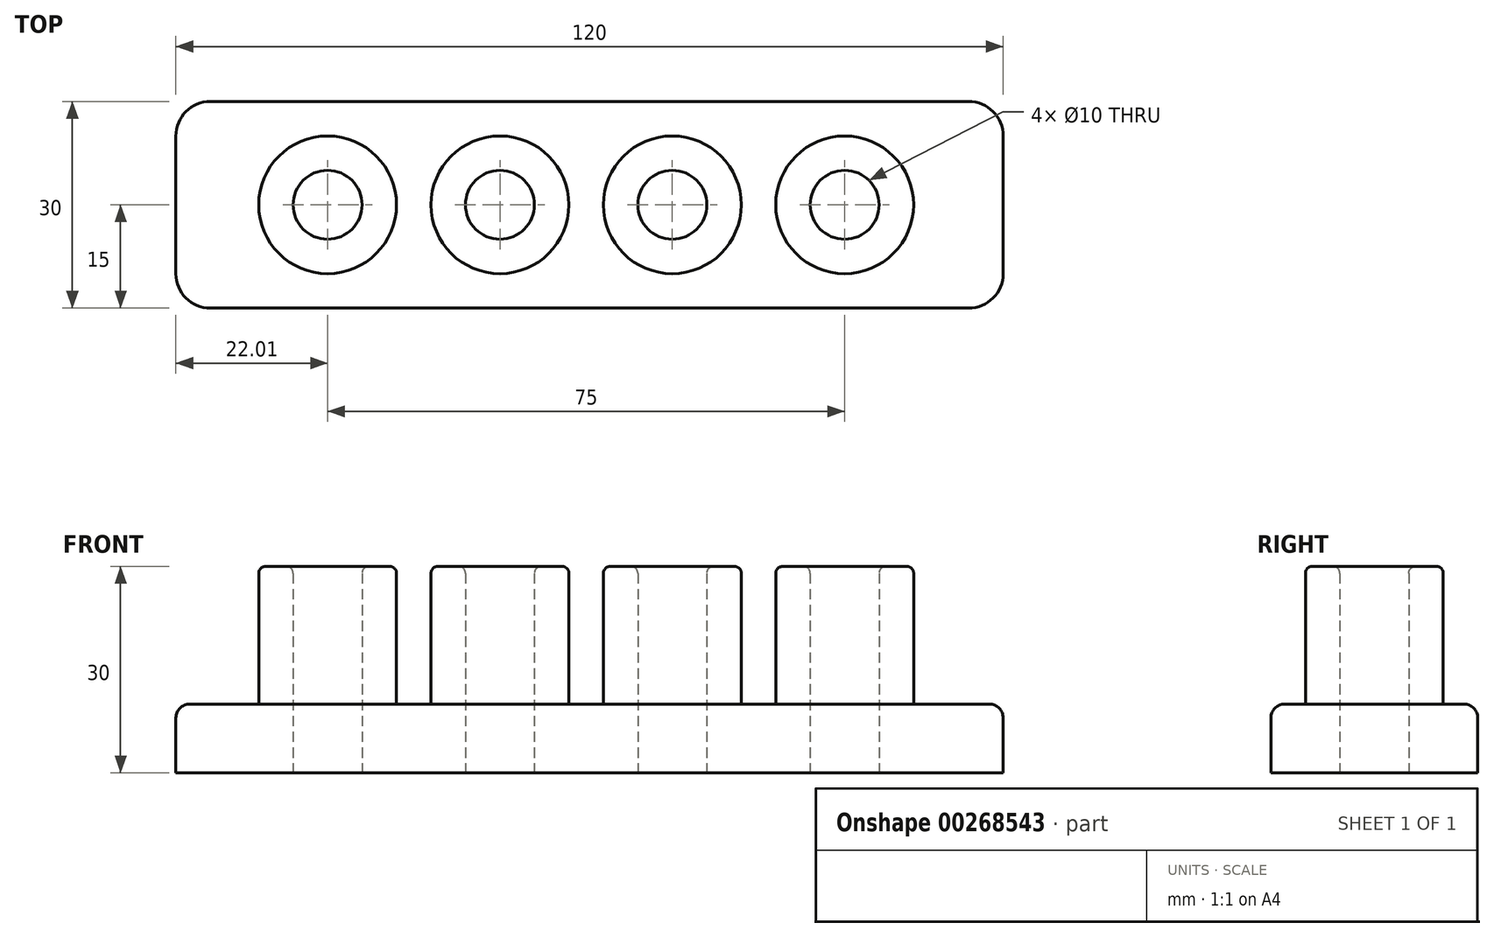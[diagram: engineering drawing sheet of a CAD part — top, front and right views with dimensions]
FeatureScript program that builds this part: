
annotation { "Feature Type Name" : "Feature", "Feature Type Description" : "" }
export const myFeature = defineFeature(function(context is Context, id is Id, definition is map)
    precondition{}
    {
        {
            var Q0;
            Q0=qCreatedBy(makeId("Top.planeOp"),FACE);
            var sketch = newSketch(context, id + "F0", { "sketchPlane" : qUnion([Q0])});
            skCircle(sketch, "E0", {"center": v(-25, 0) * mm, "radius": 10 * mm});
            skCircle(sketch, "E1", {"center": v(0, 0) * mm, "radius": 10 * mm});
            skCircle(sketch, "E2", {"center": v(25, 0) * mm, "radius": 10 * mm});
            skCircle(sketch, "E3", {"center": v(50, 0) * mm, "radius": 10 * mm});
            skLineSegment(sketch, "E4.bottom", {"start": v(-47, 15) * mm, "end": v(73, 15) * mm});
            skLineSegment(sketch, "E4.top", {"start": v(-47, -15) * mm, "end": v(73, -15) * mm});
            skLineSegment(sketch, "E4.left", {"start": v(-47, 15) * mm, "end": v(-47, -15) * mm});
            skLineSegment(sketch, "E4.right", {"start": v(73, 15) * mm, "end": v(73, -15) * mm});
            skCircle(sketch, "E5", {"center": v(-25, 0) * mm, "radius": 5 * mm});
            skCircle(sketch, "E6", {"center": v(0, 0) * mm, "radius": 5 * mm});
            skCircle(sketch, "E7", {"center": v(25, 0) * mm, "radius": 5 * mm});
            skCircle(sketch, "E8", {"center": v(50, 0) * mm, "radius": 5 * mm});
            skSolve(sketch);
        }
        {
            var Q0;
            Q0=makeQuery(id+"F0.imprint","IMPRINT",FACE,{"disambiguationData":[TD([[makeQuery(id+"F0.imprint","IMPRINT",EDGE,{"derivedFrom":sQuery(id+"F0.wireOp",EDGE,"E0")}),-1.0]])]});
            extrude(context, id + "F1", {"entities" : qUnion([Q0]), "depth" : 10 * mm});
        }
        {
            var Q0;
            Q0=makeQuery(id+"F0.imprint","IMPRINT",FACE,{"disambiguationData":[TD([[makeQuery(id+"F0.imprint","IMPRINT",EDGE,{"derivedFrom":sQuery(id+"F0.wireOp",EDGE,"E0")}),1.0]])]});
            var Q1;
            Q1=makeQuery(id+"F0.imprint","IMPRINT",FACE,{"disambiguationData":[TD([[makeQuery(id+"F0.imprint","IMPRINT",EDGE,{"derivedFrom":sQuery(id+"F0.wireOp",EDGE,"E1")}),1.0]])]});
            var Q2;
            Q2=makeQuery(id+"F0.imprint","IMPRINT",FACE,{"disambiguationData":[TD([[makeQuery(id+"F0.imprint","IMPRINT",EDGE,{"derivedFrom":sQuery(id+"F0.wireOp",EDGE,"E2")}),1.0]])]});
            var Q3;
            Q3=makeQuery(id+"F0.imprint","IMPRINT",FACE,{"disambiguationData":[TD([[makeQuery(id+"F0.imprint","IMPRINT",EDGE,{"derivedFrom":sQuery(id+"F0.wireOp",EDGE,"E3")}),1.0]])]});
            extrude(context, id + "F2", {"entities" : qUnion([Q0, Q1, Q2, Q3]), "operationType" : NewBodyOperationType.ADD, "depth" : 30 * mm});
        }
        {
            var Q0;
            Q0=makeQuery(id+"F1.opExtrude","SWEPT_EDGE",EDGE,{"disambiguationData":[OSD([sQuery(id+"F0.wireOp",EDGE,"E4.top"),sQuery(id+"F0.wireOp",EDGE,"E4.left")])]});
            var Q1;
            Q1=makeQuery(id+"F1.opExtrude","SWEPT_EDGE",EDGE,{"disambiguationData":[OSD([sQuery(id+"F0.wireOp",EDGE,"E4.bottom"),sQuery(id+"F0.wireOp",EDGE,"E4.left")])]});
            var Q2;
            Q2=makeQuery(id+"F1.opExtrude","SWEPT_EDGE",EDGE,{"disambiguationData":[OSD([sQuery(id+"F0.wireOp",EDGE,"E4.top"),sQuery(id+"F0.wireOp",EDGE,"E4.right")])]});
            var Q3;
            Q3=makeQuery(id+"F1.opExtrude","SWEPT_EDGE",EDGE,{"disambiguationData":[OSD([sQuery(id+"F0.wireOp",EDGE,"E4.bottom"),sQuery(id+"F0.wireOp",EDGE,"E4.right")])]});
            fillet(context, id + "F3", {"entities" : qUnion([Q0, Q1, Q2, Q3]), "radius" : 5 * mm, "tangentPropagation" : true, "allowEdgeOverflow" : false});
        }
        {
            var Q0;
            Q0=makeQuery(id+"F1.opExtrude","CAP_EDGE",EDGE,{"disambiguationData":[OSD([sQuery(id+"F0.wireOp",EDGE,"E4.top")])],"isStart":false});
            fillet(context, id + "F4", {"entities" : qUnion([Q0]), "radius" : 2 * mm, "tangentPropagation" : true, "allowEdgeOverflow" : false});
        }
        {
            var Q0;
            Q0=makeQuery(id+"F2.opExtrude","CAP_FACE",FACE,{"disambiguationData":[OSD([sQuery(id+"F0.wireOp",EDGE,"E0")])],"isStart":false});
            var Q1;
            Q1=makeQuery(id+"F2.opExtrude","CAP_FACE",FACE,{"disambiguationData":[OSD([sQuery(id+"F0.wireOp",EDGE,"E1")])],"isStart":false});
            var Q2;
            Q2=makeQuery(id+"F2.opExtrude","CAP_FACE",FACE,{"disambiguationData":[OSD([sQuery(id+"F0.wireOp",EDGE,"E2")])],"isStart":false});
            var Q3;
            Q3=makeQuery(id+"F2.opExtrude","CAP_FACE",FACE,{"disambiguationData":[OSD([sQuery(id+"F0.wireOp",EDGE,"E3")])],"isStart":false});
            fillet(context, id + "F5", {"entities" : qUnion([Q0, Q1, Q2, Q3]), "radius" : 1 * mm, "tangentPropagation" : true, "allowEdgeOverflow" : false});
        }
    });
